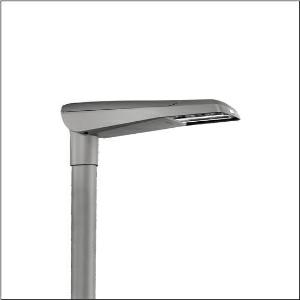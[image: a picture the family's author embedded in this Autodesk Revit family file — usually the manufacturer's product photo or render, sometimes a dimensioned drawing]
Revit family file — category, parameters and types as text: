
# Revit family: streetlight_sl_11_iq_micro___st0_5a_5xc1b41e08ce_6374
name_source: partatom
category: Lighting Fixtures
units: mm (PartAtom-declared; Revit-internal decimal feet)

## family parameters
Cut with Voids When Loaded = No
Host = Face
Light Source = No
Part Type = Normal
Room Calculation Point = No
Round Connector Dimension = Use Diameter
Shared = No

## types (1)
- --- (1 x LED, 1940 lm, 12.6 W, 4000K)
    Apparent Load = 13 VA
    CIE Flux Codes = 42 72 97 100 100
    Color Rendering = 70
    Color Temperature = 4000K
    Default Elevation = 1800 mm
    Description = Streetlight SL 11 iQ micro, mast luminaire, primary light control with 3 zone facetted reflector, of plastic, silver coated, highly specular, primary optical cover: cover, of PMMA, transparent, light distribution: ST0.5a, light emission: direct distribution, primary light characteristic: asymmetric, installation type: post-top, side-entry, lamps: LED, High Power LED, rated values: 1.940lm | 12,6W | 154lm/W (begin service life); end service life: 1.940lm | 12,9W; at 50% lumin. flux: 970lm | 6,8W | 142,6lm/W, colour temperature: 4000K, colour rendering: CRI > 70, light colour: 740, light setting 1 begin service life: 100% | 1.940lm | 12,6W | 154lm/W | 4.000K, light setting 1 end service life: 12,9W, further light settings possible, control: optimised constant luminous flux control (CLO 2.0), Desk-Remote (wireless, voltage-free reading and setting of iQ features in the workshop via application-optimized NFC function/RFID function), Light-Fading, Smart-Wire, Night-Set, Lumen-Switch, Temp-Guard, Auto-Match, with cable H07RN-F 3x 1.5mm², mains connection: 230..240V, AC, 50/60Hz, connection cable pre-assembled, cable length: 5,5m, luminaire housing, of diecast aluminium, powder-coated, SITECO metallic grey (DB 702S), please order mast flange separately, inclination adjustable without tools: 0°, 5°, 10°, 15° (post-top) | 0°, -5°, -10°, -15° (side-entry), sealing non-destructively replaceable, multi-level sealing system, length: 600mm, width: 174mm, height: 116mm, mast flange for spigot size: 42mm (side-entry): 5XC10008XM4, 60/48mm (side-entry/post-top): 5XC10108XM2, 76/60mm (side-entry/post-top): 5XC10108XM1, equipment: standard, protection rating (complete): IP66, insulation class (complete): insulation class II (safety insulation), certification: CE, ENEC, ENEC+, VDE, impact resistance: IK10, permissible operating ambient temperature for outdoor applications: -25..+50°C, standard-compliant lighting for roads and squares, Environmental Product Declaration (EPD) tested and certified by an independent institute, packaging unit: 1 piece

Light Distribution: ST0.5a
    Height = 116 mm
    Lamp = 1 x LED
    Lamp Light Flux = 1940 lm
    Lamp Power = 12.6 W
    Lamp count = 1
    Length = 600 mm
    Luminous efficacy = 154 lm/W
    Manufacturer = Siteco
    ModVariant = No
    Model = 5XC1B41E08CE
    Mounting Place = Pole
    Mounting Type = Pole top
    Number of Poles = 1
    OnlyDefault = Yes
    Power Factor = 1
    Product Name = Streetlight SL 11 iQ micro | ST0.5a
    Product group = mast luminaire | pylon top
    ProductGroupID = 6100
    Protection Class = Protection class II
    Protection Degree = IP 66
    RLX_Detail_Level = 1
    RLX_Emergency_Light_Flux = 0 lm
    RLX_Emergency_Type = 0
    RLX_Emergency_Type_DB = No
    RlxData = <blob elided: 26773 chars, md5=c2cfb459>
    Socket = socket
    Standby Power = 0 W
    System Light Flux = 1940 lm
    System Power = 13 W
    Type Comments = factory setting: luminous flux: 100 % | dim-lin: 254 | 229 mA
    Type Image = l_1006566.jpg
    URL = http://relux.com
    VarID = @adj_023415
    Voltage = 0 V
    Weight = 0.00 kg
    Width = 174 mm

## geometry (parser evidence)
native form markers: Blend x4, Sweep x11
no freeform markers — native parametric forms only
